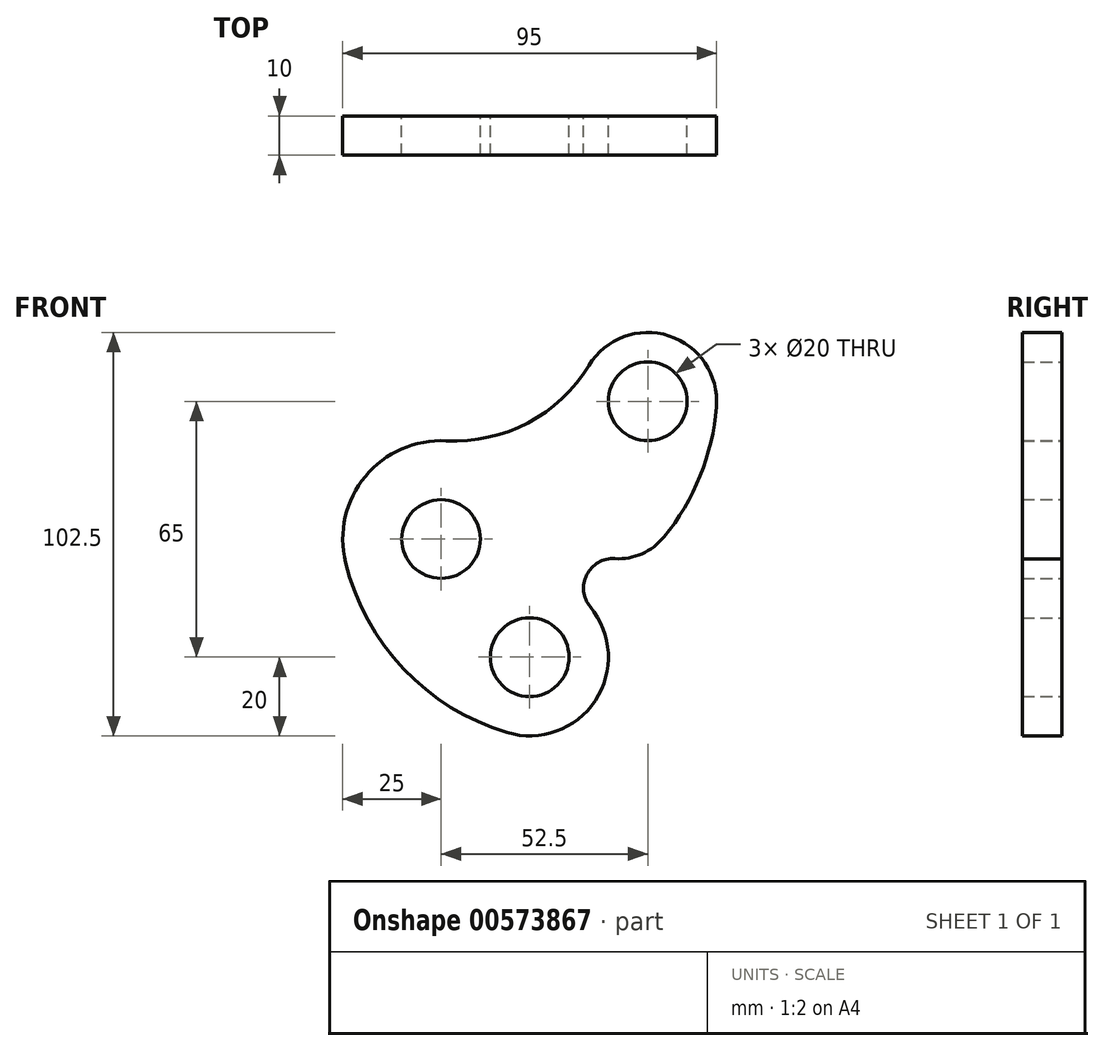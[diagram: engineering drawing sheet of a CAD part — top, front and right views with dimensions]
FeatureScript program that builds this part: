
annotation { "Feature Type Name" : "Feature", "Feature Type Description" : "" }
export const myFeature = defineFeature(function(context is Context, id is Id, definition is map)
    precondition{}
    {
        {
            var Q0;
            Q0=qCreatedBy(makeId("Front.planeOp"),FACE);
            var sketch = newSketch(context, id + "F0", { "sketchPlane" : qUnion([Q0])});
            skCircle(sketch, "E0", {"center": v(0, 0) * mm, "radius": 10 * mm});
            skCircle(sketch, "E1", {"center": v(22.5, -30) * mm, "radius": 10 * mm});
            skCircle(sketch, "E2", {"center": v(52.5, 35) * mm, "radius": 10 * mm});
            skArc(sketch, "E3", {"start": v(1.3, 24.97) * mm, "mid": v(-19.26, 15.94) * mm, "end": v(-24.28, -5.94) * mm});
            skArc(sketch, "E4", {"start": v(16.75, -49.16) * mm, "mid": v(39.17, -41.05) * mm, "end": v(37.9, -17.24) * mm});
            skArc(sketch, "E5", {"start": v(69.94, 33.58) * mm, "mid": v(57.9, 51.64) * mm, "end": v(37.55, 44.1) * mm});
            skArc(sketch, "E6", {"start": v(-24.28, -5.94) * mm, "mid": v(-9.51, -33) * mm, "end": v(16.75, -49.16) * mm});
            skArc(sketch, "E7", {"start": v(1.3, 24.97) * mm, "mid": v(22.07, 29.54) * mm, "end": v(37.55, 44.1) * mm});
            skArc(sketch, "E8", {"start": v(44.12, -4.97) * mm, "mid": v(51.03, -3.73) * mm, "end": v(56.62, 0.51) * mm});
            skArc(sketch, "E9", {"start": v(44.12, -4.97) * mm, "mid": v(37, -9.07) * mm, "end": v(37.9, -17.24) * mm});
            skArc(sketch, "E10", {"start": v(56.62, 0.51) * mm, "mid": v(65.8, 16.03) * mm, "end": v(69.94, 33.58) * mm});
            skSolve(sketch);
        }
        {
            var Q0;
            Q0=makeQuery(id+"F0.imprint","IMPRINT",FACE,{"disambiguationData":[TD([[makeQuery(id+"F0.imprint","IMPRINT",EDGE,{"derivedFrom":sQuery(id+"F0.wireOp",EDGE,"E0")}),-1.0]])]});
            extrude(context, id + "F1", {"entities" : qUnion([Q0]), "depth" : 10 * mm, "offsetDistance" : 25 * mm});
        }
    });
